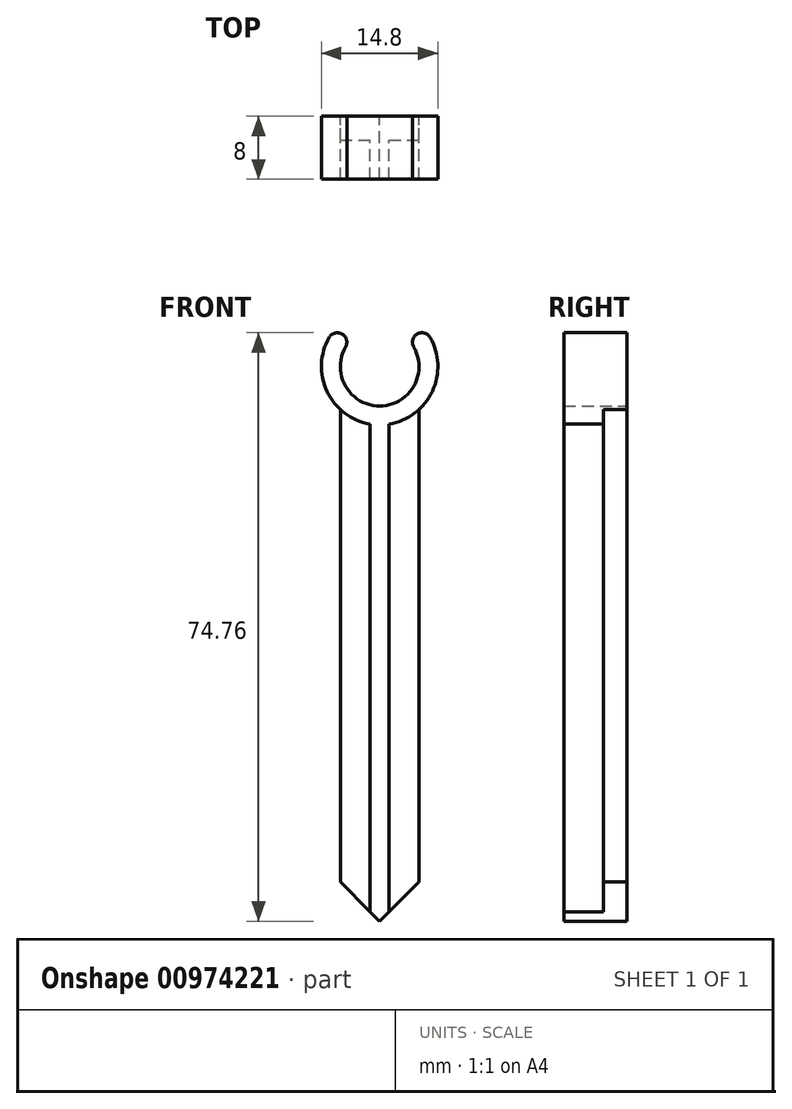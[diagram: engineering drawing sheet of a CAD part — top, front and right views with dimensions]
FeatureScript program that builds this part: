
annotation { "Feature Type Name" : "Feature", "Feature Type Description" : "" }
export const myFeature = defineFeature(function(context is Context, id is Id, definition is map)
    precondition{}
    {
        {
            var Q0;
            Q0=qCreatedBy(makeId("Front.planeOp"),FACE);
            var sketch = newSketch(context, id + "F0", { "sketchPlane" : qUnion([Q0])});
            skCircle(sketch, "E0", {"center": v(0, 0) * mm, "radius": 5 * mm});
            skCircle(sketch, "E1", {"center": v(0, 0) * mm, "radius": 7.4 * mm});
            skLineSegment(sketch, "E2", {"start": v(-5, -5.46) * mm, "end": v(-5, -65.46) * mm});
            skLineSegment(sketch, "E3", {"start": v(-5, -65.46) * mm, "end": v(0, -70.46) * mm});
            skLineSegment(sketch, "E4", {"start": v(0, -70.46) * mm, "end": v(5, -65.46) * mm});
            skLineSegment(sketch, "E5", {"start": v(5, -65.46) * mm, "end": v(5, -5.46) * mm});
            skArc(sketch, "E6", {"start": v(-4.33, 2.5) * mm, "mid": v(-4.77, 4.14) * mm, "end": v(-6.4, 3.7) * mm});
            skArc(sketch, "E7", {"start": v(6.4, 3.7) * mm, "mid": v(4.77, 4.14) * mm, "end": v(4.33, 2.5) * mm});
            skLineSegment(sketch, "E8", {"start": v(0, 0) * mm, "end": v(-15.23, 8.8) * mm, "construction": true});
            skLineSegment(sketch, "E9", {"start": v(15.23, 8.8) * mm, "end": v(0, 0) * mm, "construction": true});
            skLineSegment(sketch, "E10", {"start": v(-1.2, -7.3) * mm, "end": v(-1.2, -69.26) * mm});
            skLineSegment(sketch, "E11", {"start": v(1.2, -69.26) * mm, "end": v(1.2, -7.3) * mm});
            skSolve(sketch);
        }
        {
            var Q0;
            {var subQ4=sQuery(id+"F0.wireOp",EDGE,"E6");Q0=makeQuery(id+"F0.imprint","IMPRINT",FACE,{"disambiguationData":[TD([[makeQuery(id+"F0.imprint","IMPRINT",EDGE,{"derivedFrom":subQ4}),1.0]])]});}
            extrude(context, id + "F1", {"entities" : qUnion([Q0]), "depth" : 8 * mm, "offsetDistance" : 25 * mm});
        }
        {
            var Q0;
            {var subQ0=sQuery(id+"F0.wireOp",EDGE,"E2");Q0=makeQuery(id+"F0.imprint","IMPRINT",FACE,{"disambiguationData":[TD([[makeQuery(id+"F0.imprint","IMPRINT",EDGE,{"derivedFrom":subQ0}),1.0]])]});}
            var Q1;
            {var subQ0=sQuery(id+"F0.wireOp",EDGE,"E5");Q1=makeQuery(id+"F0.imprint","IMPRINT",FACE,{"disambiguationData":[TD([[makeQuery(id+"F0.imprint","IMPRINT",EDGE,{"derivedFrom":subQ0}),1.0]])]});}
            var Q2;
            {var subQ0=sQuery(id+"F0.wireOp",EDGE,"E10");Q2=makeQuery(id+"F0.imprint","IMPRINT",FACE,{"disambiguationData":[TD([[makeQuery(id+"F0.imprint","IMPRINT",EDGE,{"derivedFrom":subQ0}),1.0]])]});}
            extrude(context, id + "F2", {"entities" : qUnion([Q0, Q1, Q2]), "operationType" : NewBodyOperationType.ADD, "depth" : 3 * mm, "offsetDistance" : 25 * mm});
        }
        {
            var Q0;
            {var subQ0=sQuery(id+"F0.wireOp",EDGE,"E10");Q0=makeQuery(id+"F0.imprint","IMPRINT",FACE,{"disambiguationData":[TD([[makeQuery(id+"F0.imprint","IMPRINT",EDGE,{"derivedFrom":subQ0}),1.0]])]});}
            extrude(context, id + "F3", {"entities" : qUnion([Q0]), "operationType" : NewBodyOperationType.ADD, "depth" : 8 * mm, "offsetDistance" : 25 * mm});
        }
    });
